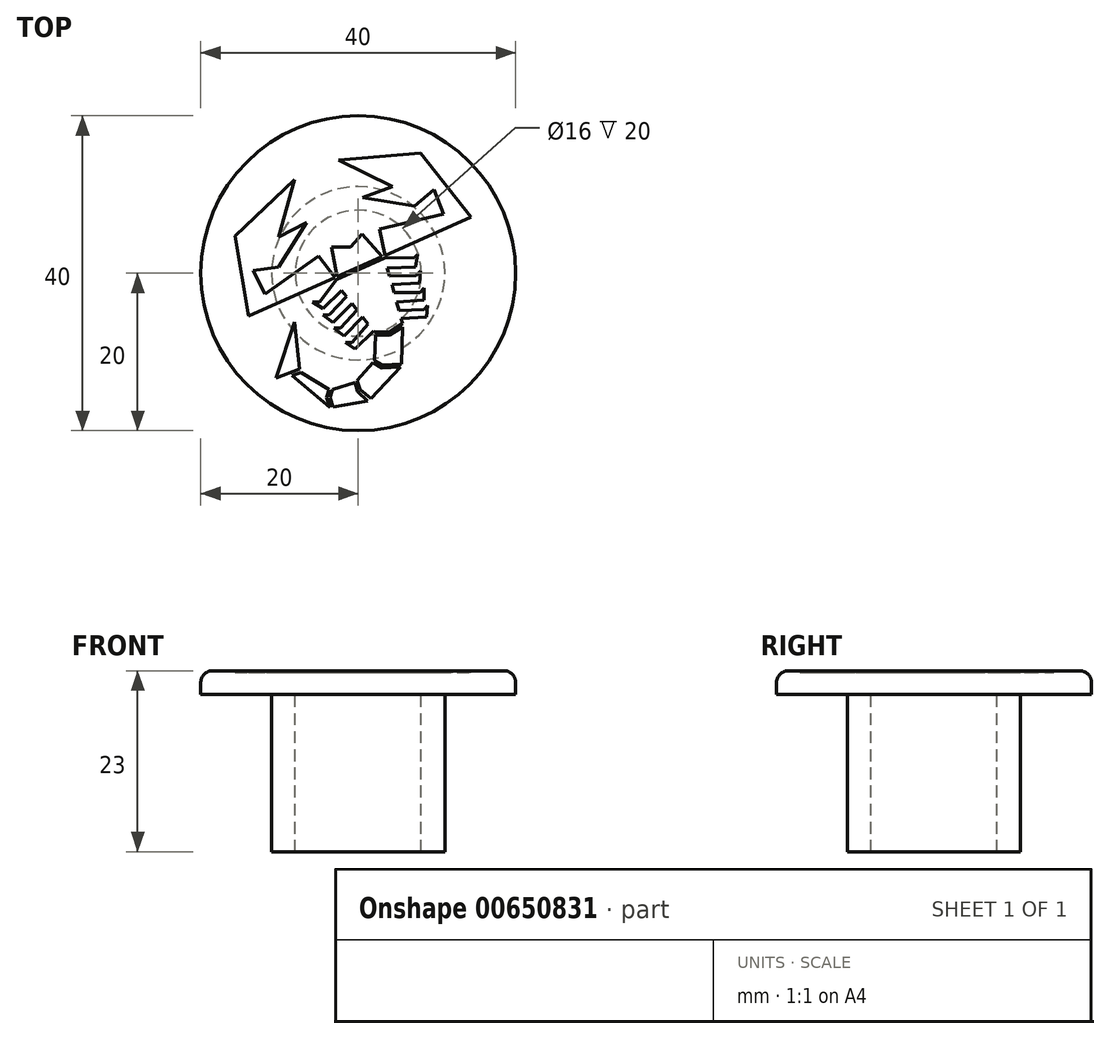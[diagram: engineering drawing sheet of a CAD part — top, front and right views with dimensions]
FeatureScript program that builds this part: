
annotation { "Feature Type Name" : "Feature", "Feature Type Description" : "" }
export const myFeature = defineFeature(function(context is Context, id is Id, definition is map)
    precondition{}
    {
        {
            var Q0;
            Q0=qCreatedBy(makeId("Top.planeOp"),FACE);
            var sketch = newSketch(context, id + "F0", { "sketchPlane" : qUnion([Q0])});
            skCircle(sketch, "E0", {"center": v(0, 0) * mm, "radius": 20 * mm});
            skSolve(sketch);
        }
        {
            var Q0;
            Q0=makeQuery(id+"F0.imprint","IMPRINT",FACE,{"disambiguationData":[TD([[makeQuery(id+"F0.imprint","IMPRINT",EDGE,{"derivedFrom":sQuery(id+"F0.wireOp",EDGE,"E0")}),1.0]])]});
            extrude(context, id + "F1", {"entities" : qUnion([Q0]), "depth" : 3 * mm, "offsetDistance" : 25 * mm});
        }
        {
            var Q0;
            Q0=makeQuery(id+"F1.opExtrude","CAP_FACE",FACE,{"disambiguationData":[OSD([sQuery(id+"F0.wireOp",EDGE,"E0")])],"isStart":true});
            var sketch = newSketch(context, id + "F2", { "sketchPlane" : qUnion([Q0])});
            skCircle(sketch, "E1", {"center": v(0, 0) * mm, "radius": 20.25 * mm});
            skSolve(sketch);
        }
        {
            var Q0;
            Q0=makeQuery(id+"F2.imprint","IMPRINT",FACE,{"disambiguationData":[TD([[makeQuery(id+"F2.imprint","IMPRINT",EDGE,{"derivedFrom":sQuery(id+"F2.wireOp",EDGE,"E1")}),1.0]])]});
            extrude(context, id + "F3", {"entities" : qUnion([Q0]), "operationType" : NewBodyOperationType.REMOVE, "oppositeDirection" : true, "depth" : 3 * mm, "offsetDistance" : 25 * mm});
        }
        {
            var Q0;
            Q0=makeQuery(id+"F1.opExtrude","CAP_FACE",FACE,{"disambiguationData":[OSD([sQuery(id+"F0.wireOp",EDGE,"E0")])],"isStart":false});
            var sketch = newSketch(context, id + "F4", { "sketchPlane" : qUnion([Q0])});
            skLineSegment(sketch, "E2.0.0", {"start": v(-10.13, 4.57) * mm, "end": v(-8.07, 11.9) * mm});
            skLineSegment(sketch, "E2.0.1", {"start": v(-8.07, 11.9) * mm, "end": v(-15.63, 4.75) * mm});
            skLineSegment(sketch, "E2.0.2", {"start": v(-15.63, 4.75) * mm, "end": v(-13.92, -5.45) * mm});
            skLineSegment(sketch, "E2.0.3", {"start": v(-13.92, -5.45) * mm, "end": v(-2.97, -0.56) * mm});
            skLineSegment(sketch, "E2.0.4", {"start": v(-2.97, -0.56) * mm, "end": v(-5.02, 2.15) * mm});
            skLineSegment(sketch, "E2.0.5", {"start": v(-5.02, 2.15) * mm, "end": v(-11.85, -2.62) * mm});
            skLineSegment(sketch, "E2.0.6", {"start": v(-11.85, -2.62) * mm, "end": v(-13.34, 0.36) * mm});
            skLineSegment(sketch, "E2.0.7", {"start": v(-13.34, 0.36) * mm, "end": v(-10.13, 0.8) * mm});
            skLineSegment(sketch, "E2.0.8", {"start": v(-10.13, 0.8) * mm, "end": v(-6.55, 6.44) * mm});
            skLineSegment(sketch, "E2.0.9", {"start": v(-6.55, 6.44) * mm, "end": v(-10.13, 4.57) * mm});
            skLineSegment(sketch, "E3.0.0", {"start": v(4.34, 11.03) * mm, "end": v(0.56, 9.62) * mm});
            skLineSegment(sketch, "E3.0.1", {"start": v(0.56, 9.62) * mm, "end": v(7.14, 8.51) * mm});
            skLineSegment(sketch, "E3.0.2", {"start": v(7.14, 8.51) * mm, "end": v(9.62, 10.6) * mm});
            skLineSegment(sketch, "E3.0.3", {"start": v(9.62, 10.6) * mm, "end": v(10.84, 7.5) * mm});
            skLineSegment(sketch, "E3.0.4", {"start": v(10.84, 7.5) * mm, "end": v(2.73, 5.6) * mm});
            skLineSegment(sketch, "E3.0.5", {"start": v(2.73, 5.6) * mm, "end": v(3.38, 2.27) * mm});
            skLineSegment(sketch, "E3.0.6", {"start": v(3.38, 2.27) * mm, "end": v(14.33, 7.16) * mm});
            skLineSegment(sketch, "E3.0.7", {"start": v(14.33, 7.16) * mm, "end": v(7.89, 15.24) * mm});
            skLineSegment(sketch, "E3.0.8", {"start": v(7.89, 15.24) * mm, "end": v(-2.49, 14.4) * mm});
            skLineSegment(sketch, "E3.0.9", {"start": v(-2.49, 14.4) * mm, "end": v(4.34, 11.03) * mm});
            skLineSegment(sketch, "E4.0.0", {"start": v(-3.4, 3.3) * mm, "end": v(-2.7, -0.44) * mm});
            skLineSegment(sketch, "E4.0.1", {"start": v(-2.7, -0.44) * mm, "end": v(3.03, 2.11) * mm});
            skLineSegment(sketch, "E4.0.2", {"start": v(3.03, 2.11) * mm, "end": v(0.46, 4.94) * mm});
            skLineSegment(sketch, "E4.0.3", {"start": v(0.46, 4.94) * mm, "end": v(-1, 3.3) * mm});
            skLineSegment(sketch, "E4.0.4", {"start": v(-1, 3.3) * mm, "end": v(-3.4, 3.3) * mm});
            skLineSegment(sketch, "E5.0.0", {"start": v(2.05, -7.47) * mm, "end": v(3.96, -7.47) * mm});
            skLineSegment(sketch, "E5.0.1", {"start": v(3.96, -7.47) * mm, "end": v(5.62, -6.42) * mm});
            skLineSegment(sketch, "E5.0.2", {"start": v(5.62, -6.42) * mm, "end": v(5.45, -5.73) * mm});
            skLineSegment(sketch, "E5.0.3", {"start": v(5.45, -5.73) * mm, "end": v(8.7, -5.56) * mm});
            skLineSegment(sketch, "E5.0.4", {"start": v(8.7, -5.56) * mm, "end": v(8.81, -4.12) * mm});
            skLineSegment(sketch, "E5.0.5", {"start": v(8.81, -4.12) * mm, "end": v(8.37, -4.62) * mm});
            skLineSegment(sketch, "E5.0.6", {"start": v(8.37, -4.62) * mm, "end": v(5.17, -4.72) * mm});
            skLineSegment(sketch, "E5.0.7", {"start": v(5.17, -4.72) * mm, "end": v(4.87, -3.64) * mm});
            skLineSegment(sketch, "E5.0.8", {"start": v(4.87, -3.64) * mm, "end": v(8.33, -3.4) * mm});
            skLineSegment(sketch, "E5.0.9", {"start": v(8.33, -3.4) * mm, "end": v(8.33, -1.89) * mm});
            skLineSegment(sketch, "E5.0.10", {"start": v(8.33, -1.89) * mm, "end": v(7.82, -2.46) * mm});
            skLineSegment(sketch, "E5.0.11", {"start": v(7.82, -2.46) * mm, "end": v(4.55, -2.46) * mm});
            skLineSegment(sketch, "E5.0.12", {"start": v(4.55, -2.46) * mm, "end": v(4.27, -1.45) * mm});
            skLineSegment(sketch, "E5.0.13", {"start": v(4.27, -1.45) * mm, "end": v(7.78, -1.25) * mm});
            skLineSegment(sketch, "E5.0.14", {"start": v(7.78, -1.25) * mm, "end": v(7.89, 0.24) * mm});
            skLineSegment(sketch, "E5.0.15", {"start": v(7.89, 0.24) * mm, "end": v(7.35, -0.28) * mm});
            skLineSegment(sketch, "E5.0.16", {"start": v(7.35, -0.28) * mm, "end": v(3.96, -0.33) * mm});
            skLineSegment(sketch, "E5.0.17", {"start": v(3.96, -0.33) * mm, "end": v(3.7, 0.65) * mm});
            skLineSegment(sketch, "E5.0.18", {"start": v(3.7, 0.65) * mm, "end": v(7.27, 0.8) * mm});
            skLineSegment(sketch, "E5.0.19", {"start": v(7.27, 0.8) * mm, "end": v(7.54, 2.39) * mm});
            skLineSegment(sketch, "E5.0.20", {"start": v(7.54, 2.39) * mm, "end": v(7.14, 1.96) * mm});
            skLineSegment(sketch, "E5.0.21", {"start": v(7.14, 1.96) * mm, "end": v(3.32, 1.9) * mm});
            skLineSegment(sketch, "E5.0.22", {"start": v(3.32, 1.9) * mm, "end": v(-2.75, -0.8) * mm});
            skLineSegment(sketch, "E5.0.23", {"start": v(-2.75, -0.8) * mm, "end": v(-4.89, -3.64) * mm});
            skLineSegment(sketch, "E5.0.24", {"start": v(-4.89, -3.64) * mm, "end": v(-5.78, -3.64) * mm});
            skLineSegment(sketch, "E5.0.25", {"start": v(-5.78, -3.64) * mm, "end": v(-4.44, -4.49) * mm});
            skLineSegment(sketch, "E5.0.26", {"start": v(-4.44, -4.49) * mm, "end": v(-2.1, -2.18) * mm});
            skLineSegment(sketch, "E5.0.27", {"start": v(-2.1, -2.18) * mm, "end": v(-1.48, -2.97) * mm});
            skLineSegment(sketch, "E5.0.28", {"start": v(-1.48, -2.97) * mm, "end": v(-3.65, -5.28) * mm});
            skLineSegment(sketch, "E5.0.29", {"start": v(-3.65, -5.28) * mm, "end": v(-4.44, -5.3) * mm});
            skLineSegment(sketch, "E5.0.30", {"start": v(-4.44, -5.3) * mm, "end": v(-3.17, -6.25) * mm});
            skLineSegment(sketch, "E5.0.31", {"start": v(-3.17, -6.25) * mm, "end": v(-0.77, -3.88) * mm});
            skLineSegment(sketch, "E5.0.32", {"start": v(-0.77, -3.88) * mm, "end": v(-0.14, -4.68) * mm});
            skLineSegment(sketch, "E5.0.33", {"start": v(-0.14, -4.68) * mm, "end": v(-2.26, -7) * mm});
            skLineSegment(sketch, "E5.0.34", {"start": v(-2.26, -7) * mm, "end": v(-3.05, -7) * mm});
            skLineSegment(sketch, "E5.0.35", {"start": v(-3.05, -7) * mm, "end": v(-1.83, -7.98) * mm});
            skLineSegment(sketch, "E5.0.36", {"start": v(-1.83, -7.98) * mm, "end": v(0.56, -5.57) * mm});
            skLineSegment(sketch, "E5.0.37", {"start": v(0.56, -5.57) * mm, "end": v(1.27, -6.48) * mm});
            skLineSegment(sketch, "E5.0.38", {"start": v(1.27, -6.48) * mm, "end": v(-0.77, -8.78) * mm});
            skLineSegment(sketch, "E5.0.39", {"start": v(-0.77, -8.78) * mm, "end": v(-1.62, -8.78) * mm});
            skLineSegment(sketch, "E5.0.40", {"start": v(-1.62, -8.78) * mm, "end": v(-0.4, -9.64) * mm});
            skLineSegment(sketch, "E5.0.41", {"start": v(-0.4, -9.64) * mm, "end": v(1.96, -7.36) * mm});
            skLineSegment(sketch, "E5.0.42", {"start": v(1.96, -7.36) * mm, "end": v(2.05, -7.47) * mm});
            skLineSegment(sketch, "E6.0.0", {"start": v(2.2, -7.86) * mm, "end": v(2.07, -11.07) * mm});
            skLineSegment(sketch, "E6.0.1", {"start": v(2.07, -11.07) * mm, "end": v(3.1, -11.68) * mm});
            skLineSegment(sketch, "E6.0.2", {"start": v(3.1, -11.68) * mm, "end": v(5.5, -11.55) * mm});
            skLineSegment(sketch, "E6.0.3", {"start": v(5.5, -11.55) * mm, "end": v(5.62, -6.82) * mm});
            skLineSegment(sketch, "E6.0.4", {"start": v(5.62, -6.82) * mm, "end": v(3.99, -7.86) * mm});
            skLineSegment(sketch, "E6.0.5", {"start": v(3.99, -7.86) * mm, "end": v(2.2, -7.86) * mm});
            skLineSegment(sketch, "E7.0.0", {"start": v(1.88, -11.34) * mm, "end": v(-0.14, -13.62) * mm});
            skLineSegment(sketch, "E7.0.1", {"start": v(-0.14, -13.62) * mm, "end": v(0.23, -14.75) * mm});
            skLineSegment(sketch, "E7.0.2", {"start": v(0.23, -14.75) * mm, "end": v(1.65, -15.93) * mm});
            skLineSegment(sketch, "E7.0.3", {"start": v(1.65, -15.93) * mm, "end": v(5.38, -11.9) * mm});
            skLineSegment(sketch, "E7.0.4", {"start": v(5.38, -11.9) * mm, "end": v(3.03, -12.03) * mm});
            skLineSegment(sketch, "E7.0.5", {"start": v(3.03, -12.03) * mm, "end": v(1.88, -11.34) * mm});
            skLineSegment(sketch, "E8.0.0", {"start": v(-0.4, -13.86) * mm, "end": v(-3.3, -14.8) * mm});
            skLineSegment(sketch, "E8.0.1", {"start": v(-3.3, -14.8) * mm, "end": v(-3.61, -15.77) * mm});
            skLineSegment(sketch, "E8.0.2", {"start": v(-3.61, -15.77) * mm, "end": v(-3.17, -16.97) * mm});
            skLineSegment(sketch, "E8.0.3", {"start": v(-3.17, -16.97) * mm, "end": v(1.2, -16.22) * mm});
            skLineSegment(sketch, "E8.0.4", {"start": v(1.2, -16.22) * mm, "end": v(-0.1, -15.03) * mm});
            skLineSegment(sketch, "E8.0.5", {"start": v(-0.1, -15.03) * mm, "end": v(-0.4, -13.86) * mm});
            skPoint(sketch, "E9.0", {"position": v(-5.98, -15.03) * mm});
            skLineSegment(sketch, "E10.0.0", {"start": v(-8.4, -13.02) * mm, "end": v(-3.57, -17.03) * mm});
            skLineSegment(sketch, "E10.0.1", {"start": v(-3.57, -17.03) * mm, "end": v(-4.04, -15.77) * mm});
            skLineSegment(sketch, "E10.0.2", {"start": v(-4.04, -15.77) * mm, "end": v(-3.7, -14.75) * mm});
            skLineSegment(sketch, "E10.0.3", {"start": v(-3.7, -14.75) * mm, "end": v(-7.28, -12.61) * mm});
            skLineSegment(sketch, "E10.0.4", {"start": v(-7.28, -12.61) * mm, "end": v(-8.4, -13.02) * mm});
            skLineSegment(sketch, "E11.0.0", {"start": v(-7.44, -12.2) * mm, "end": v(-8.07, -6.19) * mm});
            skLineSegment(sketch, "E11.0.1", {"start": v(-8.07, -6.19) * mm, "end": v(-10.42, -13.3) * mm});
            skLineSegment(sketch, "E11.0.2", {"start": v(-10.42, -13.3) * mm, "end": v(-7.44, -12.2) * mm});
            skCircle(sketch, "E12", {"center": v(0, 0) * mm, "radius": 17.92 * mm, "construction": true});
            skSolve(sketch);
        }
        {
            var Q0;
            Q0 = qSketchRegion(id + "F4", true);
            extrude(context, id + "F5", {"entities" : qUnion([Q0]), "operationType" : NewBodyOperationType.REMOVE, "oppositeDirection" : true, "depth" : .2 * mm, "offsetDistance" : 25 * mm});
        }
        {
            var Q0;
            Q0=makeQuery(id+"F1.opExtrude","CAP_EDGE",EDGE,{"disambiguationData":[OSD([sQuery(id+"F0.wireOp",EDGE,"E0")])],"isStart":false});
            fillet(context, id + "F6", {"entities" : qUnion([Q0]), "radius" : 1.5 * mm, "tangentPropagation" : true, "allowEdgeOverflow" : false});
        }
        {
            var Q0;
            Q0=makeQuery(id+"F1.opExtrude","CAP_FACE",FACE,{"disambiguationData":[OSD([sQuery(id+"F0.wireOp",EDGE,"E0")])],"isStart":true});
            var sketch = newSketch(context, id + "F7", { "sketchPlane" : qUnion([Q0])});
            skCircle(sketch, "E13", {"center": v(0, 0) * mm, "radius": 11 * mm});
            skCircle(sketch, "E14", {"center": v(0, 0) * mm, "radius": 8 * mm});
            skSolve(sketch);
        }
        {
            var Q0;
            Q0=makeQuery(id+"F7.imprint","IMPRINT",FACE,{"disambiguationData":[TD([[makeQuery(id+"F7.imprint","IMPRINT",EDGE,{"derivedFrom":sQuery(id+"F7.wireOp",EDGE,"E13")}),1.0]])]});
            extrude(context, id + "F8", {"entities" : qUnion([Q0]), "operationType" : NewBodyOperationType.ADD, "depth" : 20 * mm, "offsetDistance" : 25 * mm});
        }
    });
